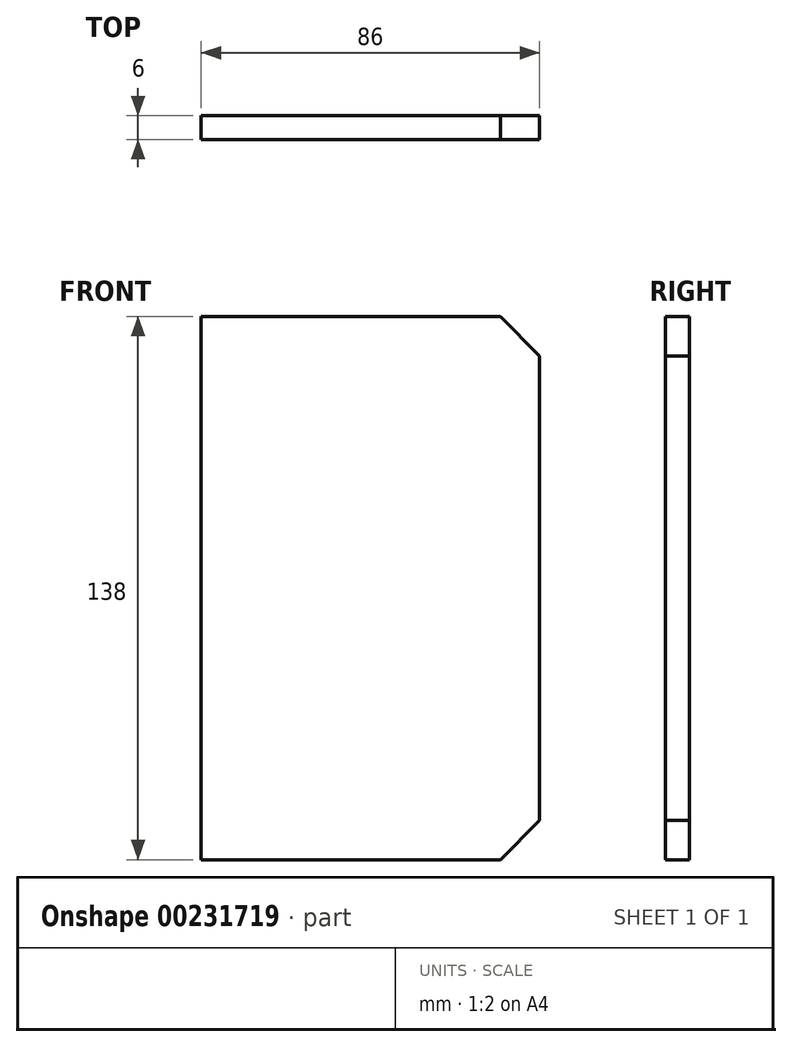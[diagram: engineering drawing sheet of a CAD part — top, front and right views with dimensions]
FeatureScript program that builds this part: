
annotation { "Feature Type Name" : "Feature", "Feature Type Description" : "" }
export const myFeature = defineFeature(function(context is Context, id is Id, definition is map)
    precondition{}
    {
        {
            var Q0;
            Q0=qCreatedBy(makeId("Front.planeOp"),FACE);
            var sketch = newSketch(context, id + "F0", { "sketchPlane" : qUnion([Q0])});
            skLineSegment(sketch, "E0.bottom", {"start": v(-53.41, 95.7) * mm, "end": v(32.59, 95.7) * mm});
            skLineSegment(sketch, "E0.top", {"start": v(-53.41, -42.3) * mm, "end": v(32.59, -42.3) * mm});
            skLineSegment(sketch, "E0.left", {"start": v(-53.41, 95.7) * mm, "end": v(-53.41, -42.3) * mm});
            skLineSegment(sketch, "E0.right", {"start": v(32.59, 95.7) * mm, "end": v(32.59, -42.3) * mm});
            skSolve(sketch);
        }
        {
            var Q0;
            Q0=makeQuery(id+"F0.imprint","IMPRINT",FACE,{"disambiguationData":[TD([[makeQuery(id+"F0.imprint","IMPRINT",EDGE,{"derivedFrom":sQuery(id+"F0.wireOp",EDGE,"E0.bottom")}),-1.0]])]});
            extrude(context, id + "F1", {"entities" : qUnion([Q0]), "depth" : 6 * mm});
        }
        {
            var Q0;
            Q0=makeQuery(id+"F1.opExtrude","SWEPT_EDGE",EDGE,{"disambiguationData":[OSD([sQuery(id+"F0.wireOp",EDGE,"E0.bottom"),sQuery(id+"F0.wireOp",EDGE,"E0.right")])]});
            var Q1;
            Q1=makeQuery(id+"F1.opExtrude","SWEPT_EDGE",EDGE,{"disambiguationData":[OSD([sQuery(id+"F0.wireOp",EDGE,"E0.top"),sQuery(id+"F0.wireOp",EDGE,"E0.right")])]});
            chamfer(context, id + "F2", {"entities" : qUnion([Q0, Q1]), "width" : 10 * mm, "tangentPropagation" : true});
        }
    });
